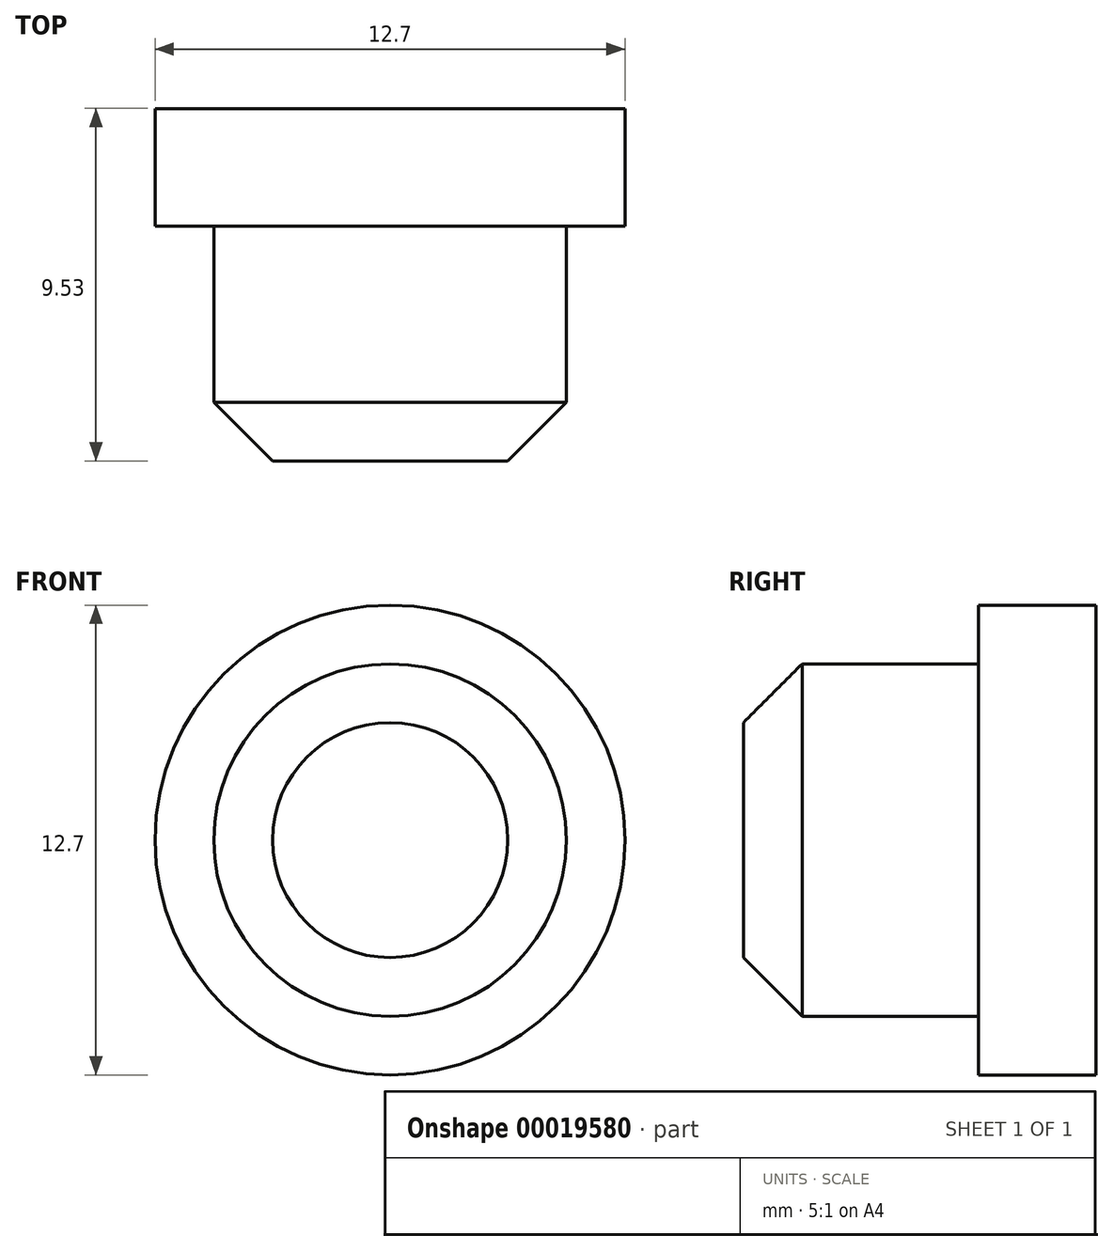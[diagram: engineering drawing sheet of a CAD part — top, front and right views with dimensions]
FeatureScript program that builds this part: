
annotation { "Feature Type Name" : "Feature", "Feature Type Description" : "" }
export const myFeature = defineFeature(function(context is Context, id is Id, definition is map)
    precondition{}
    {
        {
            var Q0;
            Q0=qCreatedBy(makeId("Top.planeOp"),FACE);
            var sketch = newSketch(context, id + "F1", { "sketchPlane" : qUnion([Q0])});
            skLineSegment(sketch, "E0.bottom", {"start": v(0, 0) * mm, "end": v(6.35, 0) * mm});
            skLineSegment(sketch, "E0.top", {"start": v(0, 3.17) * mm, "end": v(6.35, 3.17) * mm});
            skLineSegment(sketch, "E0.left", {"start": v(0, 0) * mm, "end": v(0, 3.17) * mm});
            skLineSegment(sketch, "E0.right", {"start": v(6.35, 0) * mm, "end": v(6.35, 3.17) * mm});
            skLineSegment(sketch, "E1.bottom", {"start": v(0, 0) * mm, "end": v(4.76, 0) * mm});
            skLineSegment(sketch, "E1.top", {"start": v(0, -6.35) * mm, "end": v(4.76, -6.35) * mm});
            skLineSegment(sketch, "E1.left", {"start": v(0, 0) * mm, "end": v(0, -6.35) * mm});
            skLineSegment(sketch, "E1.right", {"start": v(4.76, 0) * mm, "end": v(4.76, -6.35) * mm});
            skSolve(sketch);
        }
        {
            var Q0;
            Q0 = qSketchRegion(id + "F1", true);
            var Q1;
            Q1=sQuery(id+"F1.wireOp",EDGE,"E1.left");
            revolve(context, id + "F2", {"entities" : qUnion([Q0]), "axis" : qUnion([Q1]), "revolveType" : RevolveType.FULL});
        }
        {
            var Q0;
            Q0=makeQuery(id+"F2.opRevolve","SWEPT_FACE",FACE,{"disambiguationData":[OSD([sQuery(id+"F1.wireOp",EDGE,"E1.top")])]});
            chamfer(context, id + "F0", {"entities" : qUnion([Q0]), "width" : 1.59 * mm, "tangentPropagation" : true});
        }
    });
